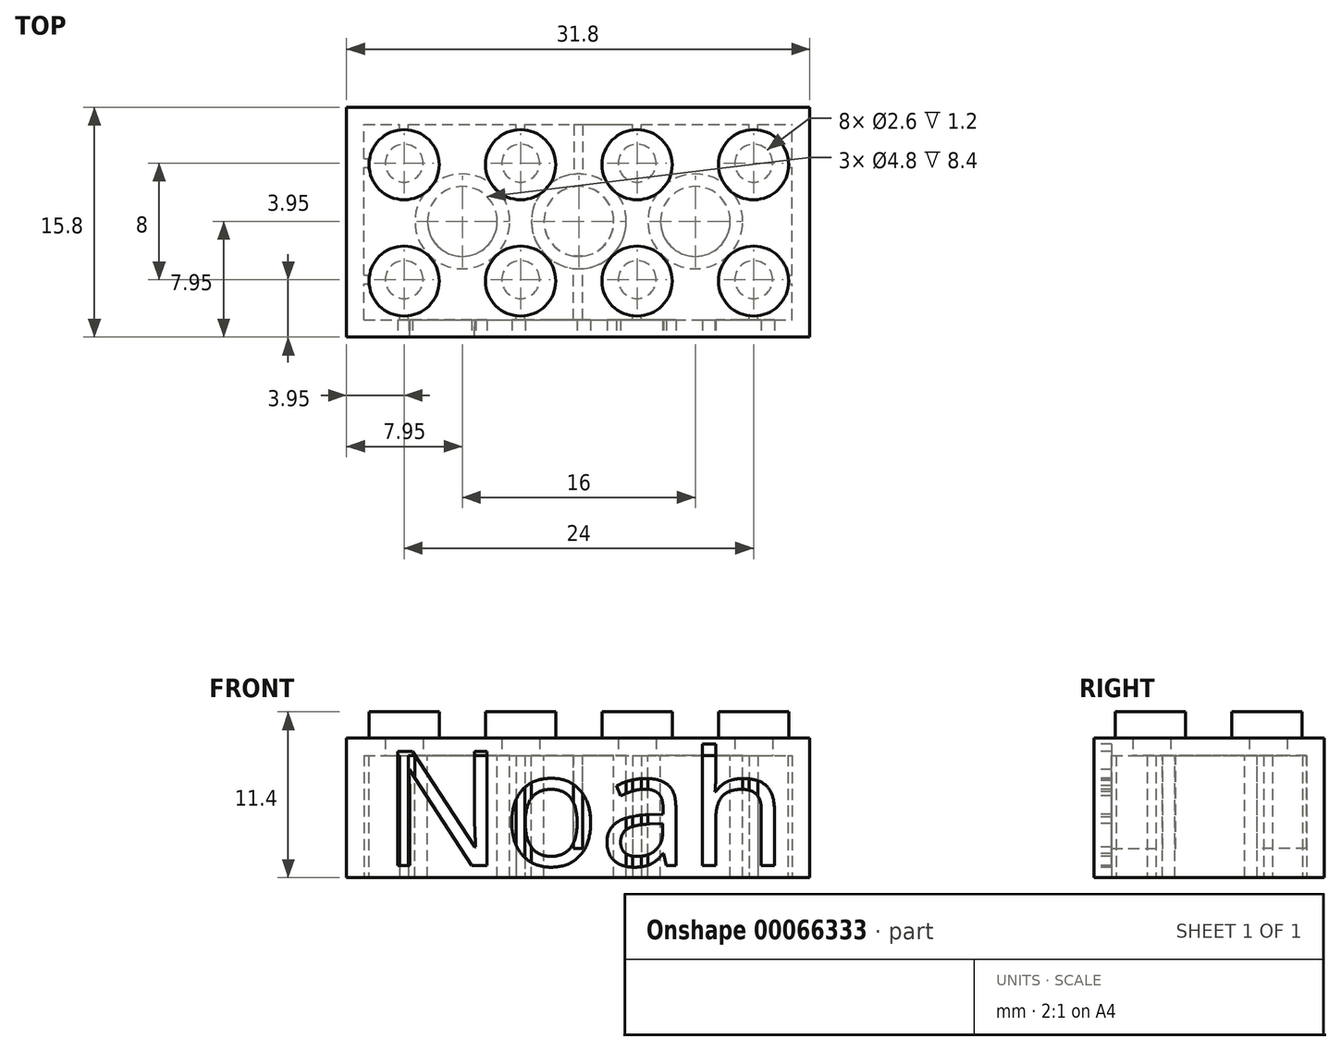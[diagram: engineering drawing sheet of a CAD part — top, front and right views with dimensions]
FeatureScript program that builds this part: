
annotation { "Feature Type Name" : "Feature", "Feature Type Description" : "" }
export const myFeature = defineFeature(function(context is Context, id is Id, definition is map)
    precondition{}
    {
        {
            var Q0;
            Q0=qCreatedBy(makeId("Top.planeOp"),FACE);
            var sketch = newSketch(context, id + "F0", { "sketchPlane" : qUnion([Q0])});
            skLineSegment(sketch, "E0.rect.bottom", {"start": v(15.9, 7.9) * mm, "end": v(-15.9, 7.9) * mm});
            skLineSegment(sketch, "E0.rect.top", {"start": v(15.9, -7.9) * mm, "end": v(-15.9, -7.9) * mm});
            skLineSegment(sketch, "E0.rect.left", {"start": v(15.9, 7.9) * mm, "end": v(15.9, -7.9) * mm});
            skLineSegment(sketch, "E0.rect.right", {"start": v(-15.9, 7.9) * mm, "end": v(-15.9, -7.9) * mm});
            skPoint(sketch, "E0.rect.middle", {"position": v(0, 0) * mm});
            skSolve(sketch);
        }
        {
            var Q0;
            Q0 = qSketchRegion(id + "F0", true);
            extrude(context, id + "F1", {"entities" : qUnion([Q0]), "depth" : 9.6 * mm});
        }
        {
            var Q0;
            Q0=qCreatedBy(makeId("Top.planeOp"),FACE);
            var sketch = newSketch(context, id + "F2", { "sketchPlane" : qUnion([Q0])});
            skLineSegment(sketch, "E1.rect.bottom", {"start": v(-14.7, -6.7) * mm, "end": v(14.7, -6.7) * mm});
            skLineSegment(sketch, "E1.rect.top", {"start": v(-14.7, 6.7) * mm, "end": v(14.7, 6.7) * mm});
            skLineSegment(sketch, "E1.rect.left", {"start": v(-14.7, -6.7) * mm, "end": v(-14.7, 6.7) * mm});
            skLineSegment(sketch, "E1.rect.right", {"start": v(14.7, -6.7) * mm, "end": v(14.7, 6.7) * mm});
            skPoint(sketch, "E1.rect.middle", {"position": v(0, 0) * mm});
            skPoint(sketch, "E2.rect.middle", {"position": v(-14.7, 0) * mm});
            skSolve(sketch);
        }
        {
            var Q0;
            Q0 = qSketchRegion(id + "F2", true);
            extrude(context, id + "F3", {"entities" : qUnion([Q0]), "operationType" : NewBodyOperationType.REMOVE, "depth" : 8.4 * mm, "offsetDistance" : 25 * mm});
        }
        {
            var Q0;
            Q0=makeQuery(id+"F1.opExtrude","CAP_FACE",FACE,{"disambiguationData":[OSD([sQuery(id+"F0.wireOp",EDGE,"E0.rect.bottom"),sQuery(id+"F0.wireOp",EDGE,"E0.rect.top"),sQuery(id+"F0.wireOp",EDGE,"E0.rect.left"),sQuery(id+"F0.wireOp",EDGE,"E0.rect.right")])],"isStart":false});
            var sketch = newSketch(context, id + "F4", { "sketchPlane" : qUnion([Q0])});
            skLineSegment(sketch, "E3", {"start": v(-15.9, 0) * mm, "end": v(15.9, 0) * mm});
            skCircle(sketch, "E4", {"center": v(-11.95, 3.95) * mm, "radius": 2.4 * mm});
            skCircle(sketch, "E5.0.1.0", {"center": v(-11.95, -4.05) * mm, "radius": 2.4 * mm});
            skCircle(sketch, "E5.1.0.0", {"center": v(-3.95, 3.95) * mm, "radius": 2.4 * mm});
            skCircle(sketch, "E5.1.1.0", {"center": v(-3.95, -4.05) * mm, "radius": 2.4 * mm});
            skCircle(sketch, "E5.2.0.0", {"center": v(4.05, 3.95) * mm, "radius": 2.4 * mm});
            skCircle(sketch, "E5.2.1.0", {"center": v(4.05, -4.05) * mm, "radius": 2.4 * mm});
            skCircle(sketch, "E5.3.0.0", {"center": v(12.05, 3.95) * mm, "radius": 2.4 * mm});
            skCircle(sketch, "E5.3.1.0", {"center": v(12.05, -4.05) * mm, "radius": 2.4 * mm});
            skLineSegment(sketch, "E5.direction1", {"start": v(-11.95, 3.95) * mm, "end": v(-3.95, 3.95) * mm, "construction": true});
            skLineSegment(sketch, "E5.direction2", {"start": v(-11.95, 3.95) * mm, "end": v(-11.95, -4.05) * mm, "construction": true});
            skSolve(sketch);
        }
        {
            var Q0;
            Q0 = qSketchRegion(id + "F4", true);
            extrude(context, id + "F5", {"entities" : qUnion([Q0]), "operationType" : NewBodyOperationType.ADD, "depth" : 1.8 * mm});
        }
        {
            var Q0;
            Q0=makeQuery(id+"F3.boolean.opBoolean","COPY",FACE,{"derivedFrom":makeQuery(id+"F3.opExtrude","CAP_FACE",FACE,{"disambiguationData":[OSD([sQuery(id+"F2.wireOp",EDGE,"E1.rect.bottom"),sQuery(id+"F2.wireOp",EDGE,"E1.rect.top"),sQuery(id+"F2.wireOp",EDGE,"E1.rect.left"),sQuery(id+"F2.wireOp",EDGE,"E1.rect.right")])],"isStart":false})});
            var sketch = newSketch(context, id + "F6", { "sketchPlane" : qUnion([Q0])});
            skCircle(sketch, "E6", {"center": v(-11.95, 3.95) * mm, "radius": 1.3 * mm});
            skCircle(sketch, "E7.0.1.0", {"center": v(-11.95, -4.05) * mm, "radius": 1.3 * mm});
            skCircle(sketch, "E7.1.0.0", {"center": v(-3.95, 3.95) * mm, "radius": 1.3 * mm});
            skCircle(sketch, "E7.1.1.0", {"center": v(-3.95, -4.05) * mm, "radius": 1.3 * mm});
            skCircle(sketch, "E7.2.0.0", {"center": v(4.05, 3.95) * mm, "radius": 1.3 * mm});
            skCircle(sketch, "E7.2.1.0", {"center": v(4.05, -4.05) * mm, "radius": 1.3 * mm});
            skCircle(sketch, "E7.3.0.0", {"center": v(12.05, 3.95) * mm, "radius": 1.3 * mm});
            skCircle(sketch, "E7.3.1.0", {"center": v(12.05, -4.05) * mm, "radius": 1.3 * mm});
            skSolve(sketch);
        }
        {
            var Q0;
            Q0 = qSketchRegion(id + "F6", true);
            extrude(context, id + "F7", {"entities" : qUnion([Q0]), "operationType" : NewBodyOperationType.REMOVE, "oppositeDirection" : true, "depth" : 1.2 * mm, "offsetDistance" : 25 * mm});
        }
        {
            var Q0;
            Q0=makeQuery(id+"F6.imprint","IMPRINT",FACE,{"disambiguationData":[TD([[makeQuery(id+"F6.imprint","IMPRINT",EDGE,{"derivedFrom":sQuery(id+"F6.wireOp",EDGE,"E6")}),-1.0]])]});
            var sketch = newSketch(context, id + "F8", { "sketchPlane" : qUnion([Q0])});
            skLineSegment(sketch, "E8", {"start": v(-3.95, 3.95) * mm, "end": v(-11.95, -4.05) * mm, "construction": true});
            skLineSegment(sketch, "E9", {"start": v(-11.95, 3.95) * mm, "end": v(-3.95, -4.05) * mm, "construction": true});
            skLineSegment(sketch, "E10", {"start": v(-3.95, 3.95) * mm, "end": v(4.05, -4.05) * mm, "construction": true});
            skLineSegment(sketch, "E11", {"start": v(4.05, -4.05) * mm, "end": v(12.05, 3.95) * mm, "construction": true});
            skLineSegment(sketch, "E12", {"start": v(-3.95, -4.05) * mm, "end": v(4.05, 3.95) * mm, "construction": true});
            skLineSegment(sketch, "E13", {"start": v(4.05, 3.95) * mm, "end": v(12.05, -4.05) * mm, "construction": true});
            skPoint(sketch, "E14.positionSnap0", {"position": v(-7.95, -0.05) * mm});
            skCircle(sketch, "E15", {"center": v(-7.95, -0.05) * mm, "radius": 2.4 * mm});
            skCircle(sketch, "E16", {"center": v(-7.95, -0.05) * mm, "radius": 3.25 * mm});
            skCircle(sketch, "E17", {"center": v(0.05, -0.05) * mm, "radius": 3.25 * mm});
            skCircle(sketch, "E18", {"center": v(0.05, -0.05) * mm, "radius": 2.4 * mm});
            skCircle(sketch, "E19", {"center": v(8.05, -0.05) * mm, "radius": 3.25 * mm});
            skCircle(sketch, "E20", {"center": v(8.05, -0.05) * mm, "radius": 2.4 * mm});
            skSolve(sketch);
        }
        {
            var Q0;
            Q0 = qSketchRegion(id + "F8", true);
            var Q1;
            Q1=makeQuery(id+"F1.opExtrude","CAP_FACE",FACE,{"disambiguationData":[OSD([sQuery(id+"F0.wireOp",EDGE,"E0.rect.bottom"),sQuery(id+"F0.wireOp",EDGE,"E0.rect.top"),sQuery(id+"F0.wireOp",EDGE,"E0.rect.left"),sQuery(id+"F0.wireOp",EDGE,"E0.rect.right")])],"isStart":true});
            extrude(context, id + "F9", {"entities" : qUnion([Q0]), "operationType" : NewBodyOperationType.ADD, "endBound" : BoundingType.UP_TO_SURFACE, "endBoundEntityFace" : qUnion([Q1]), "depth" : 25 * mm, "offsetDistance" : 25 * mm});
        }
        {
            var Q0;
            Q0=makeQuery(id+"F1.opExtrude","CAP_FACE",FACE,{"disambiguationData":[OSD([sQuery(id+"F0.wireOp",EDGE,"E0.rect.bottom"),sQuery(id+"F0.wireOp",EDGE,"E0.rect.top"),sQuery(id+"F0.wireOp",EDGE,"E0.rect.left"),sQuery(id+"F0.wireOp",EDGE,"E0.rect.right")])],"isStart":true});
            var sketch = newSketch(context, id + "F10", { "sketchPlane" : qUnion([Q0])});
            skLineSegment(sketch, "E21.bottom", {"start": v(-12.25, 6.7) * mm, "end": v(-11.65, 6.7) * mm});
            skLineSegment(sketch, "E21.top", {"start": v(-12.25, 6.4) * mm, "end": v(-11.65, 6.4) * mm});
            skLineSegment(sketch, "E21.left", {"start": v(-12.25, 6.7) * mm, "end": v(-12.25, 6.4) * mm});
            skLineSegment(sketch, "E21.right", {"start": v(-11.65, 6.7) * mm, "end": v(-11.65, 6.4) * mm});
            skLineSegment(sketch, "E22", {"start": v(-11.95, 24.12) * mm, "end": v(-11.95, -4.05) * mm, "construction": true});
            skLineSegment(sketch, "E23.0.1.0", {"start": v(-12.25, -6.4) * mm, "end": v(-11.65, -6.4) * mm});
            skLineSegment(sketch, "E23.0.1.1", {"start": v(-12.25, -6.4) * mm, "end": v(-12.25, -6.7) * mm});
            skLineSegment(sketch, "E23.0.1.2", {"start": v(-12.25, -6.7) * mm, "end": v(-11.65, -6.7) * mm});
            skLineSegment(sketch, "E23.0.1.3", {"start": v(-11.65, -6.4) * mm, "end": v(-11.65, -6.7) * mm});
            skLineSegment(sketch, "E23.1.0.0", {"start": v(-4.25, 6.7) * mm, "end": v(-3.65, 6.7) * mm});
            skLineSegment(sketch, "E23.1.0.1", {"start": v(-4.25, 6.7) * mm, "end": v(-4.25, 6.4) * mm});
            skLineSegment(sketch, "E23.1.0.2", {"start": v(-4.25, 6.4) * mm, "end": v(-3.65, 6.4) * mm});
            skLineSegment(sketch, "E23.1.0.3", {"start": v(-3.65, 6.7) * mm, "end": v(-3.65, 6.4) * mm});
            skLineSegment(sketch, "E23.1.1.0", {"start": v(-4.25, -6.4) * mm, "end": v(-3.65, -6.4) * mm});
            skLineSegment(sketch, "E23.1.1.1", {"start": v(-4.25, -6.4) * mm, "end": v(-4.25, -6.7) * mm});
            skLineSegment(sketch, "E23.1.1.2", {"start": v(-4.25, -6.7) * mm, "end": v(-3.65, -6.7) * mm});
            skLineSegment(sketch, "E23.1.1.3", {"start": v(-3.65, -6.4) * mm, "end": v(-3.65, -6.7) * mm});
            skLineSegment(sketch, "E23.2.0.0", {"start": v(3.75, 6.7) * mm, "end": v(4.35, 6.7) * mm});
            skLineSegment(sketch, "E23.2.0.1", {"start": v(3.75, 6.7) * mm, "end": v(3.75, 6.4) * mm});
            skLineSegment(sketch, "E23.2.0.2", {"start": v(3.75, 6.4) * mm, "end": v(4.35, 6.4) * mm});
            skLineSegment(sketch, "E23.2.0.3", {"start": v(4.35, 6.7) * mm, "end": v(4.35, 6.4) * mm});
            skLineSegment(sketch, "E23.2.1.0", {"start": v(3.75, -6.4) * mm, "end": v(4.35, -6.4) * mm});
            skLineSegment(sketch, "E23.2.1.1", {"start": v(3.75, -6.4) * mm, "end": v(3.75, -6.7) * mm});
            skLineSegment(sketch, "E23.2.1.2", {"start": v(3.75, -6.7) * mm, "end": v(4.35, -6.7) * mm});
            skLineSegment(sketch, "E23.2.1.3", {"start": v(4.35, -6.4) * mm, "end": v(4.35, -6.7) * mm});
            skLineSegment(sketch, "E23.3.0.0", {"start": v(11.75, 6.7) * mm, "end": v(12.35, 6.7) * mm});
            skLineSegment(sketch, "E23.3.0.1", {"start": v(11.75, 6.7) * mm, "end": v(11.75, 6.4) * mm});
            skLineSegment(sketch, "E23.3.0.2", {"start": v(11.75, 6.4) * mm, "end": v(12.35, 6.4) * mm});
            skLineSegment(sketch, "E23.3.0.3", {"start": v(12.35, 6.7) * mm, "end": v(12.35, 6.4) * mm});
            skLineSegment(sketch, "E23.3.1.0", {"start": v(11.75, -6.4) * mm, "end": v(12.35, -6.4) * mm});
            skLineSegment(sketch, "E23.3.1.1", {"start": v(11.75, -6.4) * mm, "end": v(11.75, -6.7) * mm});
            skLineSegment(sketch, "E23.3.1.2", {"start": v(11.75, -6.7) * mm, "end": v(12.35, -6.7) * mm});
            skLineSegment(sketch, "E23.3.1.3", {"start": v(12.35, -6.4) * mm, "end": v(12.35, -6.7) * mm});
            skLineSegment(sketch, "E23.direction1", {"start": v(-12.25, 6.7) * mm, "end": v(-4.25, 6.7) * mm, "construction": true});
            skLineSegment(sketch, "E23.direction2", {"start": v(-12.25, 6.7) * mm, "end": v(-12.25, -6.4) * mm, "construction": true});
            skSolve(sketch);
        }
        {
            var Q0;
            Q0 = qSketchRegion(id + "F10", true);
            var Q1;
            {var subQ0=sQuery(id+"F2.wireOp",EDGE,"E1.rect.bottom");var subQ1=sQuery(id+"F2.wireOp",EDGE,"E1.rect.top");var subQ2=sQuery(id+"F2.wireOp",EDGE,"E1.rect.left");var subQ3=sQuery(id+"F2.wireOp",EDGE,"E1.rect.right");Q1=makeQuery(id+"F9.boolean.opBoolean","SPLIT",FACE,{"disambiguationData":[TD([makeQuery(id+"F3.boolean.opBoolean","COPY",FACE,{"derivedFrom":makeQuery(id+"F3.opExtrude","SWEPT_FACE",FACE,{"disambiguationData":[OSD([subQ0])]})})])],"derivedFrom":makeQuery(id+"F3.boolean.opBoolean","COPY",FACE,{"derivedFrom":makeQuery(id+"F3.opExtrude","CAP_FACE",FACE,{"disambiguationData":[OSD([subQ0,subQ1,subQ2,subQ3])],"isStart":false})})});}
            extrude(context, id + "F11", {"entities" : qUnion([Q0]), "operationType" : NewBodyOperationType.ADD, "endBound" : BoundingType.UP_TO_SURFACE, "oppositeDirection" : true, "endBoundEntityFace" : qUnion([Q1]), "depth" : 25 * mm});
        }
        {
            var Q0;
            Q0=makeQuery(id+"F11.boolean.opBoolean","MERGE",FACE,{"derivedFrom":[makeQuery(id+"F1.opExtrude","CAP_FACE",FACE,{"disambiguationData":[OSD([sQuery(id+"F0.wireOp",EDGE,"E0.rect.bottom"),sQuery(id+"F0.wireOp",EDGE,"E0.rect.top"),sQuery(id+"F0.wireOp",EDGE,"E0.rect.left"),sQuery(id+"F0.wireOp",EDGE,"E0.rect.right")])],"isStart":true}),makeQuery(id+"F11.opExtrude","CAP_FACE",FACE,{"disambiguationData":[OSD([sQuery(id+"F10.wireOp",EDGE,"E21.bottom"),sQuery(id+"F10.wireOp",EDGE,"E21.top"),sQuery(id+"F10.wireOp",EDGE,"E21.left"),sQuery(id+"F10.wireOp",EDGE,"E21.right")])],"isStart":true}),makeQuery(id+"F11.opExtrude","CAP_FACE",FACE,{"disambiguationData":[OSD([sQuery(id+"F10.wireOp",EDGE,"E23.0.1.0"),sQuery(id+"F10.wireOp",EDGE,"E23.0.1.1"),sQuery(id+"F10.wireOp",EDGE,"E23.0.1.2"),sQuery(id+"F10.wireOp",EDGE,"E23.0.1.3")])],"isStart":true}),makeQuery(id+"F11.opExtrude","CAP_FACE",FACE,{"disambiguationData":[OSD([sQuery(id+"F10.wireOp",EDGE,"E23.1.0.0"),sQuery(id+"F10.wireOp",EDGE,"E23.1.0.1"),sQuery(id+"F10.wireOp",EDGE,"E23.1.0.2"),sQuery(id+"F10.wireOp",EDGE,"E23.1.0.3")])],"isStart":true}),makeQuery(id+"F11.opExtrude","CAP_FACE",FACE,{"disambiguationData":[OSD([sQuery(id+"F10.wireOp",EDGE,"E23.1.1.0"),sQuery(id+"F10.wireOp",EDGE,"E23.1.1.1"),sQuery(id+"F10.wireOp",EDGE,"E23.1.1.2"),sQuery(id+"F10.wireOp",EDGE,"E23.1.1.3")])],"isStart":true}),makeQuery(id+"F11.opExtrude","CAP_FACE",FACE,{"disambiguationData":[OSD([sQuery(id+"F10.wireOp",EDGE,"E23.2.0.0"),sQuery(id+"F10.wireOp",EDGE,"E23.2.0.1"),sQuery(id+"F10.wireOp",EDGE,"E23.2.0.2"),sQuery(id+"F10.wireOp",EDGE,"E23.2.0.3")])],"isStart":true}),makeQuery(id+"F11.opExtrude","CAP_FACE",FACE,{"disambiguationData":[OSD([sQuery(id+"F10.wireOp",EDGE,"E23.2.1.0"),sQuery(id+"F10.wireOp",EDGE,"E23.2.1.1"),sQuery(id+"F10.wireOp",EDGE,"E23.2.1.2"),sQuery(id+"F10.wireOp",EDGE,"E23.2.1.3")])],"isStart":true}),makeQuery(id+"F11.opExtrude","CAP_FACE",FACE,{"disambiguationData":[OSD([sQuery(id+"F10.wireOp",EDGE,"E23.3.0.0"),sQuery(id+"F10.wireOp",EDGE,"E23.3.0.1"),sQuery(id+"F10.wireOp",EDGE,"E23.3.0.2"),sQuery(id+"F10.wireOp",EDGE,"E23.3.0.3")])],"isStart":true}),makeQuery(id+"F11.opExtrude","CAP_FACE",FACE,{"disambiguationData":[OSD([sQuery(id+"F10.wireOp",EDGE,"E23.3.1.0"),sQuery(id+"F10.wireOp",EDGE,"E23.3.1.1"),sQuery(id+"F10.wireOp",EDGE,"E23.3.1.2"),sQuery(id+"F10.wireOp",EDGE,"E23.3.1.3")])],"isStart":true})]});
            var sketch = newSketch(context, id + "F12", { "sketchPlane" : qUnion([Q0])});
            skLineSegment(sketch, "E24", {"start": v(-16.18, 3.95) * mm, "end": v(-11.95, 3.95) * mm, "construction": true});
            skLineSegment(sketch, "E25.bottom", {"start": v(-14.7, 4.25) * mm, "end": v(-14.4, 4.25) * mm});
            skLineSegment(sketch, "E25.top", {"start": v(-14.7, 3.65) * mm, "end": v(-14.4, 3.65) * mm});
            skLineSegment(sketch, "E25.left", {"start": v(-14.7, 4.25) * mm, "end": v(-14.7, 3.65) * mm});
            skLineSegment(sketch, "E25.right", {"start": v(-14.4, 4.25) * mm, "end": v(-14.4, 3.65) * mm});
            skLineSegment(sketch, "E26.0.1.0", {"start": v(-14.7, -4.35) * mm, "end": v(-14.4, -4.35) * mm});
            skLineSegment(sketch, "E26.0.1.1", {"start": v(-14.4, -3.75) * mm, "end": v(-14.4, -4.35) * mm});
            skLineSegment(sketch, "E26.0.1.2", {"start": v(-14.7, -3.75) * mm, "end": v(-14.7, -4.35) * mm});
            skLineSegment(sketch, "E26.0.1.3", {"start": v(-14.7, -3.75) * mm, "end": v(-14.4, -3.75) * mm});
            skLineSegment(sketch, "E26.1.0.0", {"start": v(14.4, 3.65) * mm, "end": v(14.7, 3.65) * mm});
            skLineSegment(sketch, "E26.1.0.1", {"start": v(14.7, 4.25) * mm, "end": v(14.7, 3.65) * mm});
            skLineSegment(sketch, "E26.1.0.2", {"start": v(14.4, 4.25) * mm, "end": v(14.4, 3.65) * mm});
            skLineSegment(sketch, "E26.1.0.3", {"start": v(14.4, 4.25) * mm, "end": v(14.7, 4.25) * mm});
            skLineSegment(sketch, "E26.1.1.0", {"start": v(14.4, -4.35) * mm, "end": v(14.7, -4.35) * mm});
            skLineSegment(sketch, "E26.1.1.1", {"start": v(14.7, -3.75) * mm, "end": v(14.7, -4.35) * mm});
            skLineSegment(sketch, "E26.1.1.2", {"start": v(14.4, -3.75) * mm, "end": v(14.4, -4.35) * mm});
            skLineSegment(sketch, "E26.1.1.3", {"start": v(14.4, -3.75) * mm, "end": v(14.7, -3.75) * mm});
            skLineSegment(sketch, "E26.direction2", {"start": v(-14.7, 3.65) * mm, "end": v(-14.7, -4.35) * mm, "construction": true});
            skSolve(sketch);
        }
        {
            var Q0;
            Q0 = qSketchRegion(id + "F12", true);
            var Q1;
            {var subQ0=sQuery(id+"F2.wireOp",EDGE,"E1.rect.bottom");var subQ1=sQuery(id+"F2.wireOp",EDGE,"E1.rect.top");var subQ2=sQuery(id+"F2.wireOp",EDGE,"E1.rect.left");var subQ3=sQuery(id+"F2.wireOp",EDGE,"E1.rect.right");Q1=makeQuery(id+"F9.boolean.opBoolean","SPLIT",FACE,{"disambiguationData":[TD([makeQuery(id+"F3.boolean.opBoolean","COPY",FACE,{"derivedFrom":makeQuery(id+"F3.opExtrude","SWEPT_FACE",FACE,{"disambiguationData":[OSD([subQ0])]})})])],"derivedFrom":makeQuery(id+"F3.boolean.opBoolean","COPY",FACE,{"derivedFrom":makeQuery(id+"F3.opExtrude","CAP_FACE",FACE,{"disambiguationData":[OSD([subQ0,subQ1,subQ2,subQ3])],"isStart":false})})});}
            extrude(context, id + "F13", {"entities" : qUnion([Q0]), "operationType" : NewBodyOperationType.ADD, "endBound" : BoundingType.UP_TO_SURFACE, "oppositeDirection" : true, "endBoundEntityFace" : qUnion([Q1]), "depth" : 25 * mm});
        }
        {
            var Q0;
            Q0=makeQuery(id+"F6.imprint","IMPRINT",FACE,{"disambiguationData":[TD([[makeQuery(id+"F6.imprint","IMPRINT",EDGE,{"derivedFrom":sQuery(id+"F6.wireOp",EDGE,"E6")}),-1.0]])]});
            var sketch = newSketch(context, id + "F14", { "sketchPlane" : qUnion([Q0])});
            skLineSegment(sketch, "E27.bottom", {"start": v(-0.33, 6.7) * mm, "end": v(0.32, 6.7) * mm});
            skLineSegment(sketch, "E27.top", {"start": v(-0.33, 2.3) * mm, "end": v(0.32, 2.3) * mm});
            skLineSegment(sketch, "E27.left", {"start": v(-0.33, 6.7) * mm, "end": v(-0.33, 2.3) * mm});
            skLineSegment(sketch, "E27.right", {"start": v(0.32, 6.7) * mm, "end": v(0.32, 2.3) * mm});
            skLineSegment(sketch, "E28.bottom", {"start": v(-0.3, -6.7) * mm, "end": v(0.3, -6.7) * mm});
            skLineSegment(sketch, "E28.top", {"start": v(-0.3, -2.7) * mm, "end": v(0.3, -2.7) * mm});
            skLineSegment(sketch, "E28.left", {"start": v(-0.3, -6.7) * mm, "end": v(-0.3, -2.7) * mm});
            skLineSegment(sketch, "E28.right", {"start": v(0.3, -6.7) * mm, "end": v(0.3, -2.7) * mm});
            skSolve(sketch);
        }
        {
            var Q0;
            Q0=makeQuery(id+"F1.opExtrude","SWEPT_FACE",FACE,{"disambiguationData":[OSD([sQuery(id+"F0.wireOp",EDGE,"E0.rect.top")])]});
            var sketch = newSketch(context, id + "F15", { "sketchPlane" : qUnion([Q0])});
            skText(sketch, "E29", { "text": "Noah", "fontName": "OpenSans-Regular.ttf"});
            const initialGuessF15  = {"E29": [-0.01348, 0.00083, 1, 0, 0.00793]};
            skSetInitialGuess(sketch, initialGuessF15);
            skSolve(sketch);
        }
        {
            var Q0;
            Q0 = qSketchRegion(id + "F15", true);
            extrude(context, id + "F16", {"entities" : qUnion([Q0]), "operationType" : NewBodyOperationType.REMOVE, "oppositeDirection" : true, "depth" : 1.2 * mm});
        }
        {
            var Q0;
            Q0 = qSketchRegion(id + "F14", true);
            extrude(context, id + "F17", {"entities" : qUnion([Q0]), "operationType" : NewBodyOperationType.ADD, "depth" : 6.4 * mm, "offsetDistance" : 25 * mm});
        }
    });
